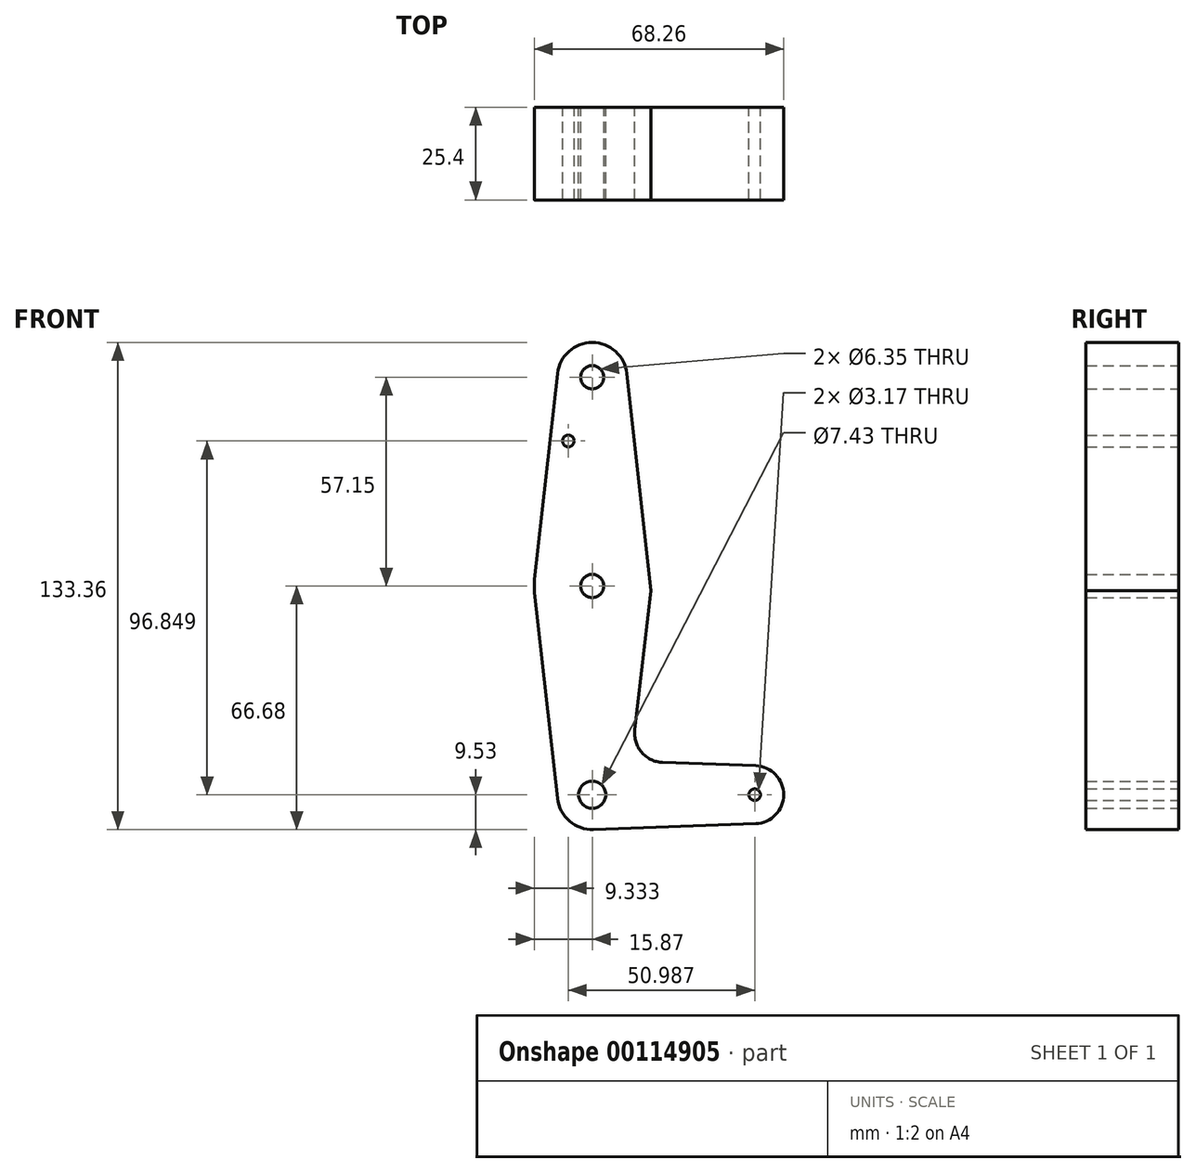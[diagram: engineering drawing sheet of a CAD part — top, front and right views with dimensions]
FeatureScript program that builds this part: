
annotation { "Feature Type Name" : "Feature", "Feature Type Description" : "" }
export const myFeature = defineFeature(function(context is Context, id is Id, definition is map)
    precondition{}
    {
        {
            var Q0;
            Q0=qCreatedBy(makeId("Front.planeOp"),FACE);
            var sketch = newSketch(context, id + "F0", { "sketchPlane" : qUnion([Q0])});
            skLineSegment(sketch, "E0", {"start": v(0, 114.3) * mm, "end": v(0, 0) * mm});
            skLineSegment(sketch, "E1", {"start": v(0, 0) * mm, "end": v(44.45, 0) * mm});
            skCircle(sketch, "E2", {"center": v(0, 114.3) * mm, "radius": 9.53 * mm});
            skCircle(sketch, "E3", {"center": v(0, 57.15) * mm, "radius": 15.88 * mm});
            skCircle(sketch, "E4", {"center": v(0, 0) * mm, "radius": 9.53 * mm});
            skCircle(sketch, "E5", {"center": v(44.45, 0) * mm, "radius": 7.94 * mm});
            skLineSegment(sketch, "E6", {"start": v(-9.47, 115.36) * mm, "end": v(-15.78, 58.91) * mm});
            skLineSegment(sketch, "E7", {"start": v(9.47, 115.36) * mm, "end": v(16.12, 55.87) * mm});
            skLineSegment(sketch, "E8", {"start": v(16.12, 55.87) * mm, "end": v(11.66, 17.7) * mm});
            skLineSegment(sketch, "E9", {"start": v(19.27, 8.84) * mm, "end": v(44.73, 7.93) * mm});
            skCircle(sketch, "E10", {"center": v(0, 114.3) * mm, "radius": 3.18 * mm});
            skCircle(sketch, "E11", {"center": v(0, 0) * mm, "radius": 3.71 * mm});
            skCircle(sketch, "E12", {"center": v(44.45, 0) * mm, "radius": 1.59 * mm});
            skCircle(sketch, "E13", {"center": v(-6.54, 96.85) * mm, "radius": 1.59 * mm});
            skCircle(sketch, "E14", {"center": v(0, 57.15) * mm, "radius": 3.18 * mm});
            skPoint(sketch, "E15.newPointB", {"position": v(0, 9.53) * mm});
            skArc(sketch, "E15.filletArc", {"start": v(11.66, 17.7) * mm, "mid": v(13.52, 11.6) * mm, "end": v(19.27, 8.84) * mm});
            skLineSegment(sketch, "E16", {"start": v(-15.78, 55.39) * mm, "end": v(-9.47, -1.06) * mm});
            skLineSegment(sketch, "E17", {"start": v(0.34, -9.52) * mm, "end": v(44.73, -7.93) * mm});
            skSolve(sketch);
        }
        {
            var Q0;
            Q0 = qSketchRegion(id + "F0", true);
            var Q1;
            {var subQ0=sQuery(id+"F0.wireOp",EDGE,"E4");var subQ1=sQuery(id+"F0.wireOp",EDGE,"E0");var subQ2=makeQuery(id+"F0.imprint","INTERSECT",VERTEX,{"derivedFrom":[subQ1,subQ0]});Q1=makeQuery(id+"F0.imprint","IMPRINT",FACE,{"disambiguationData":[TD([[makeQuery(id+"F0.imprint","IMPRINT",EDGE,{"disambiguationData":[TD([[subQ2,-1.0]])],"derivedFrom":subQ1}),1.0]])]});}
            extrude(context, id + "F1", {"entities" : qUnion([Q0, Q1]), "depth" : 25.4 * mm});
        }
    });
